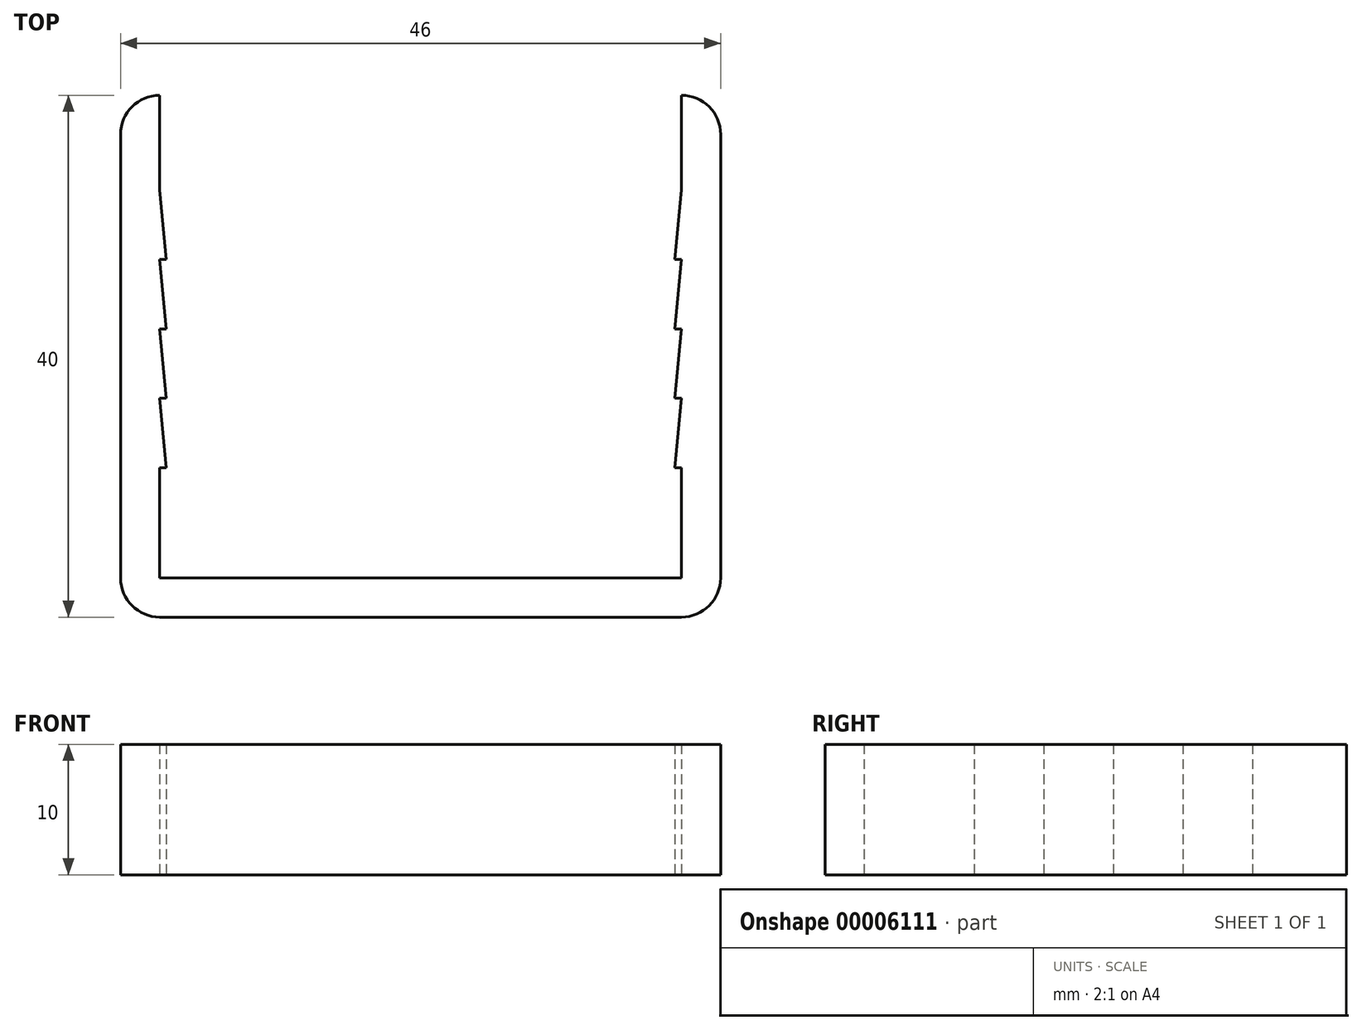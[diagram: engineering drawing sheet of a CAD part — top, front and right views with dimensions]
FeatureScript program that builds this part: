
annotation { "Feature Type Name" : "Feature", "Feature Type Description" : "" }
export const myFeature = defineFeature(function(context is Context, id is Id, definition is map)
    precondition{}
    {
        {
            var Q0;
            Q0=qCreatedBy(makeId("Top.planeOp"),FACE);
            var sketch = newSketch(context, id + "F0", { "sketchPlane" : qUnion([Q0])});
            skLineSegment(sketch, "E0", {"start": v(0, 0) * mm, "end": v(23, 0) * mm});
            skLineSegment(sketch, "E1", {"start": v(23, 0) * mm, "end": v(23, 40) * mm});
            skLineSegment(sketch, "E2", {"start": v(0, 0) * mm, "end": v(0, 3) * mm});
            skLineSegment(sketch, "E3", {"start": v(0, 3) * mm, "end": v(20, 3) * mm});
            skLineSegment(sketch, "E4", {"start": v(20, 3) * mm, "end": v(20, 40) * mm});
            skLineSegment(sketch, "E5", {"start": v(20, 40) * mm, "end": v(23, 40) * mm});
            skLineSegment(sketch, "E6.0.MirrorCS", {"start": v(0, 3) * mm, "end": v(-20, 3) * mm});
            skLineSegment(sketch, "E7.0.MirrorCS", {"start": v(0, 0) * mm, "end": v(-23, 0) * mm});
            skLineSegment(sketch, "E8.0.MirrorCS", {"start": v(-23, 0) * mm, "end": v(-23, 40) * mm});
            skLineSegment(sketch, "E9.0.MirrorCS", {"start": v(-20, 3) * mm, "end": v(-20, 40) * mm});
            skLineSegment(sketch, "E10.0.MirrorCS", {"start": v(-20, 40) * mm, "end": v(-23, 40) * mm});
            skLineSegment(sketch, "E11", {"start": v(20, 32.76) * mm, "end": v(19.5, 27.43) * mm});
            skLineSegment(sketch, "E12", {"start": v(19.5, 27.43) * mm, "end": v(20, 27.43) * mm});
            skLineSegment(sketch, "E13.1.0.0", {"start": v(20, 27.43) * mm, "end": v(19.5, 22.1) * mm});
            skLineSegment(sketch, "E13.1.0.1", {"start": v(19.5, 22.1) * mm, "end": v(20, 22.1) * mm});
            skLineSegment(sketch, "E13.2.0.0", {"start": v(20, 22.1) * mm, "end": v(19.5, 16.77) * mm});
            skLineSegment(sketch, "E13.2.0.1", {"start": v(19.5, 16.77) * mm, "end": v(20, 16.77) * mm});
            skLineSegment(sketch, "E13.direction1", {"start": v(19.5, 27.43) * mm, "end": v(19.5, 22.1) * mm, "construction": true});
            skLineSegment(sketch, "E14.0.3.0", {"start": v(20, 16.77) * mm, "end": v(19.5, 11.43) * mm});
            skLineSegment(sketch, "E14.3.3.0", {"start": v(19.5, 11.43) * mm, "end": v(20, 11.43) * mm});
            skLineSegment(sketch, "E15.0.MirrorCS", {"start": v(-20, 32.76) * mm, "end": v(-19.5, 27.43) * mm});
            skLineSegment(sketch, "E16.0.MirrorCS", {"start": v(-20, 27.43) * mm, "end": v(-19.5, 27.43) * mm});
            skLineSegment(sketch, "E17.0.MirrorCS", {"start": v(-20, 27.43) * mm, "end": v(-19.5, 22.1) * mm});
            skLineSegment(sketch, "E18.0.MirrorCS", {"start": v(-20, 22.1) * mm, "end": v(-19.5, 22.1) * mm});
            skLineSegment(sketch, "E19.0.MirrorCS", {"start": v(-20, 22.1) * mm, "end": v(-19.5, 16.77) * mm});
            skLineSegment(sketch, "E20.0.MirrorCS", {"start": v(-20, 16.77) * mm, "end": v(-19.5, 11.43) * mm});
            skLineSegment(sketch, "E21.0.MirrorCS", {"start": v(-20, 16.77) * mm, "end": v(-19.5, 16.77) * mm});
            skLineSegment(sketch, "E22.0.MirrorCS", {"start": v(-20, 11.43) * mm, "end": v(-19.5, 11.43) * mm});
            skSolve(sketch);
        }
        {
            var Q0;
            Q0 = qSketchRegion(id + "F0", true);
            extrude(context, id + "F1", {"entities" : qUnion([Q0]), "depth" : 10 * mm});
        }
        {
            var Q0;
            Q0=makeQuery(id+"F1.opExtrude","SWEPT_EDGE",EDGE,{"disambiguationData":[OSD([sQuery(id+"F0.wireOp",EDGE,"E7.0.MirrorCS"),sQuery(id+"F0.wireOp",EDGE,"E8.0.MirrorCS")])]});
            var Q1;
            Q1=makeQuery(id+"F1.opExtrude","SWEPT_EDGE",EDGE,{"disambiguationData":[OSD([sQuery(id+"F0.wireOp",EDGE,"E0"),sQuery(id+"F0.wireOp",EDGE,"E1")])]});
            var Q2;
            Q2=makeQuery(id+"F1.opExtrude","SWEPT_EDGE",EDGE,{"disambiguationData":[OSD([sQuery(id+"F0.wireOp",EDGE,"E8.0.MirrorCS"),sQuery(id+"F0.wireOp",EDGE,"E10.0.MirrorCS")])]});
            var Q3;
            Q3=makeQuery(id+"F1.opExtrude","SWEPT_EDGE",EDGE,{"disambiguationData":[OSD([sQuery(id+"F0.wireOp",EDGE,"E1"),sQuery(id+"F0.wireOp",EDGE,"E5")])]});
            fillet(context, id + "F2", {"entities" : qUnion([Q0, Q1, Q2, Q3]), "radius" : 3 * mm, "tangentPropagation" : true, "allowEdgeOverflow" : false});
        }
    });
